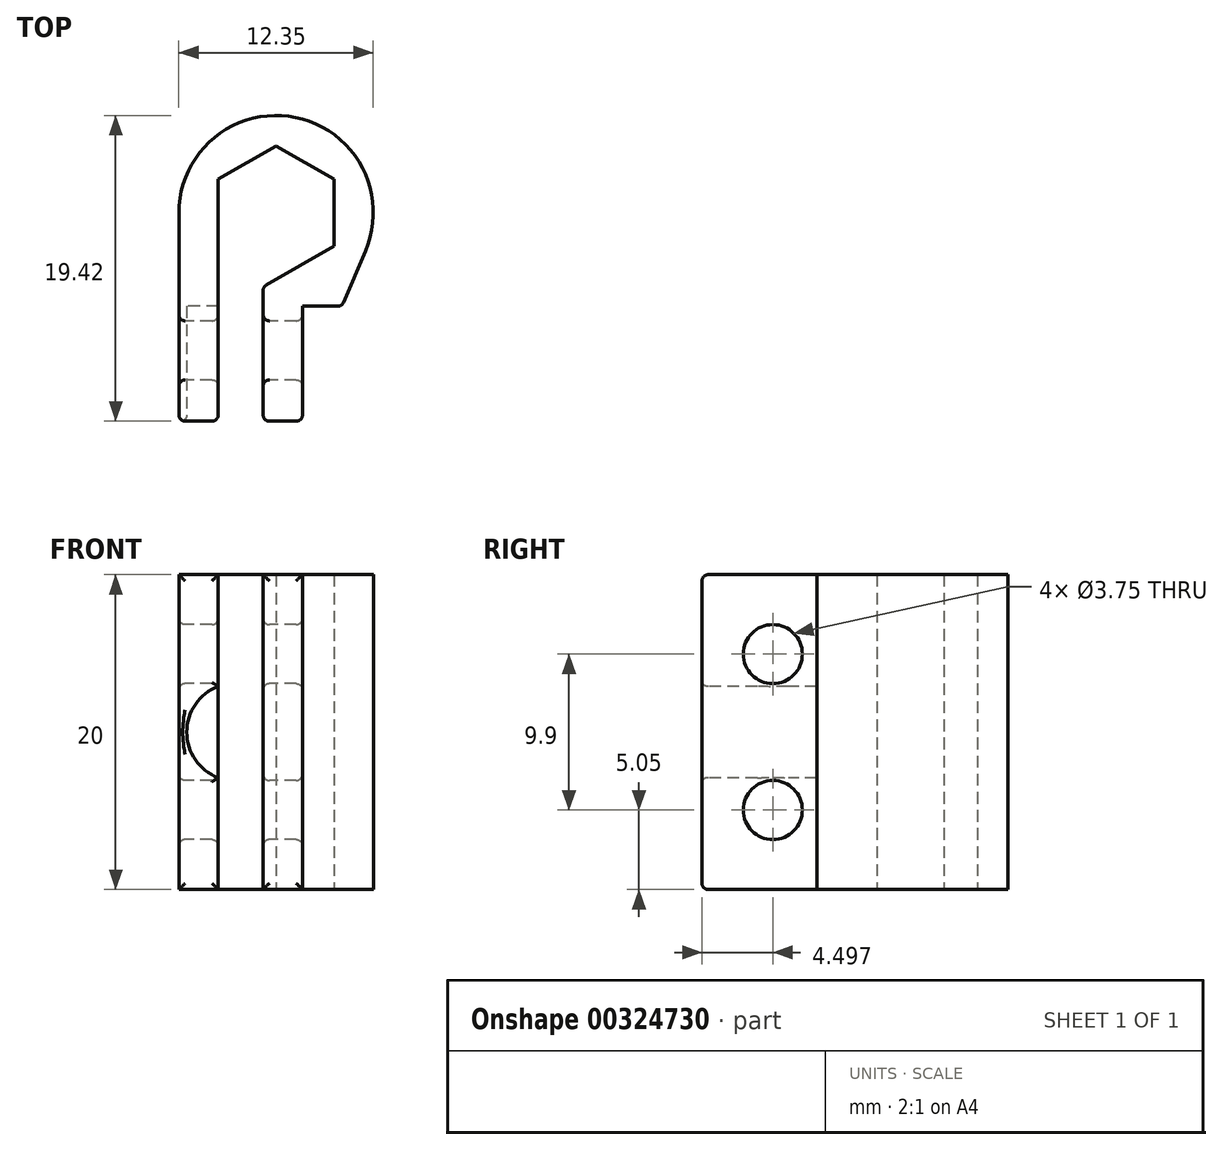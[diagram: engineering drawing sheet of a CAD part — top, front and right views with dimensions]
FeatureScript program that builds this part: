
annotation { "Feature Type Name" : "Feature", "Feature Type Description" : "" }
export const myFeature = defineFeature(function(context is Context, id is Id, definition is map)
    precondition{}
    {
        {
            var Q0;
            Q0=qCreatedBy(makeId("Top.planeOp"),FACE);
            var sketch = newSketch(context, id + "F0", { "sketchPlane" : qUnion([Q0])});
            skCircle(sketch, "E0", {"center": v(0, 0) * mm, "radius": 3.67 * mm, "construction": true});
            skArc(sketch, "E1.0", {"start": v(-0.82, -6.12) * mm, "mid": v(2.32, 5.72) * mm, "end": v(-3.67, -4.96) * mm});
            skLineSegment(sketch, "E2", {"start": v(-6.17, 0) * mm, "end": v(-6.17, -13.24) * mm});
            skLineSegment(sketch, "E3", {"start": v(-6.17, -13.24) * mm, "end": v(-3.67, -13.24) * mm});
            skLineSegment(sketch, "E4", {"start": v(-3.67, -13.24) * mm, "end": v(-3.67, 0) * mm});
            skLineSegment(sketch, "E5", {"start": v(-3.67, -13.24) * mm, "end": v(-0.82, -13.24) * mm, "construction": true});
            skLineSegment(sketch, "E6", {"start": v(-0.82, -13.24) * mm, "end": v(-0.82, -4.72) * mm});
            skLineSegment(sketch, "E7", {"start": v(-0.82, -13.24) * mm, "end": v(1.67, -13.24) * mm});
            skLineSegment(sketch, "E8", {"start": v(1.68, -13.24) * mm, "end": v(1.68, -5.94) * mm});
            skPoint(sketch, "E9", {"position": v(-6.17, -10.24) * mm});
            skPoint(sketch, "E10", {"position": v(-6.17, -7.24) * mm});
            skPoint(sketch, "E11", {"position": v(-6.17, -8.74) * mm});
            skLineSegment(sketch, "E12", {"start": v(-6.17, -7.24) * mm, "end": v(-6.17, -10.24) * mm});
            skLineSegment(sketch, "E13", {"start": v(-6.17, -8.74) * mm, "end": v(1.68, -8.74) * mm, "construction": true});
            skPoint(sketch, "E14", {"position": v(1.68, -5.94) * mm});
            skPoint(sketch, "E15", {"position": v(1.68, -11.54) * mm});
            skLineSegment(sketch, "E16.0", {"start": v(-3.67, -2.12) * mm, "end": v(-3.67, 2.12) * mm});
            skLineSegment(sketch, "E16.1", {"start": v(-3.68, 2.12) * mm, "end": v(0, 4.24) * mm});
            skLineSegment(sketch, "E16.2", {"start": v(0, 4.24) * mm, "end": v(3.68, 2.12) * mm});
            skLineSegment(sketch, "E16.3", {"start": v(3.67, 2.12) * mm, "end": v(3.67, -2.12) * mm});
            skLineSegment(sketch, "E16.4", {"start": v(3.68, -2.12) * mm, "end": v(-0.82, -4.72) * mm});
            skPoint(sketch, "E16.0.midPoint", {"position": v(-3.67, 0) * mm});
            skLineSegment(sketch, "E17", {"start": v(1.67, -5.94) * mm, "end": v(4.17, -5.94) * mm});
            skLineSegment(sketch, "E18", {"start": v(4.17, -5.94) * mm, "end": v(5.68, -2.43) * mm});
            skSolve(sketch);
        }
        {
            var Q0;
            Q0=qSketchRegion(id+"F0",true);
            extrude(context, id + "F1", {"entities" : qUnion([Q0]), "depth" : 20 * mm});
        }
        {
            var Q0;
            Q0=makeQuery(id+"F1.opExtrude","SWEPT_FACE",FACE,{"disambiguationData":[OSD([sQuery(id+"F0.wireOp",EDGE,"E2"),sQuery(id+"F0.wireOp",EDGE,"E12")])]});
            var sketch = newSketch(context, id + "F2", { "sketchPlane" : qUnion([Q0])});
            skPoint(sketch, "E19.0", {"position": v(8.74, 0) * mm});
            skLineSegment(sketch, "E20", {"start": v(8.74, 0) * mm, "end": v(8.74, 20) * mm, "construction": true});
            skPoint(sketch, "E21", {"position": v(8.74, 10) * mm});
            skPoint(sketch, "E22", {"position": v(8.74, 12.9) * mm});
            skPoint(sketch, "E23", {"position": v(8.74, 7.1) * mm});
            skPoint(sketch, "E24", {"position": v(8.74, 17) * mm});
            skPoint(sketch, "E25", {"position": v(8.74, 3) * mm});
            skPoint(sketch, "E26", {"position": v(8.74, 14.95) * mm});
            skPoint(sketch, "E27", {"position": v(8.74, 5.05) * mm});
            skCircle(sketch, "E28", {"center": v(8.74, 14.95) * mm, "radius": 1.88 * mm});
            skCircle(sketch, "E29", {"center": v(8.74, 5.05) * mm, "radius": 1.88 * mm});
            skSolve(sketch);
        }
        {
            var Q0;
            Q0=makeQuery(id+"F2.imprint","IMPRINT",FACE,{"disambiguationData":[TD([[makeQuery(id+"F2.imprint","IMPRINT",EDGE,{"derivedFrom":sQuery(id+"F2.wireOp",EDGE,"E28")}),1.0]])]});
            var Q1;
            Q1=makeQuery(id+"F2.imprint","IMPRINT",FACE,{"disambiguationData":[TD([[makeQuery(id+"F2.imprint","IMPRINT",EDGE,{"derivedFrom":sQuery(id+"F2.wireOp",EDGE,"E29")}),1.0]])]});
            extrude(context, id + "F3", {"entities" : qUnion([Q0, Q1]), "operationType" : NewBodyOperationType.REMOVE, "endBound" : BoundingType.THROUGH_ALL, "oppositeDirection" : true, "depth" : 25.4 * mm});
        }
        {
            var Q0;
            Q0=makeQuery(id+"F1.opExtrude","SWEPT_FACE",FACE,{"disambiguationData":[OSD([sQuery(id+"F0.wireOp",EDGE,"E3")])]});
            var sketch = newSketch(context, id + "F4", { "sketchPlane" : qUnion([Q0])});
            skPoint(sketch, "E30.0", {"position": v(-6.17, 7.1) * mm});
            skPoint(sketch, "E30.1", {"position": v(-6.17, 12.9) * mm});
            skPoint(sketch, "E30.2", {"position": v(-6.17, 10) * mm});
            skLineSegment(sketch, "E31", {"start": v(-6.17, 10) * mm, "end": v(-3.67, 10) * mm, "construction": true});
            skLineSegment(sketch, "E32", {"start": v(-6.17, 12.9) * mm, "end": v(-3.67, 12.9) * mm, "construction": true});
            skLineSegment(sketch, "E33", {"start": v(-6.17, 7.1) * mm, "end": v(-3.67, 7.1) * mm});
            skArc(sketch, "E34", {"start": v(-3.67, 12.9) * mm, "mid": v(-5.67, 10) * mm, "end": v(-3.67, 7.1) * mm});
            skPoint(sketch, "E35", {"position": v(-5.67, 10) * mm});
            skSolve(sketch);
        }
        {
            var Q0;
            {var subQ0=sQuery(id+"F4.wireOp",EDGE,"E34");Q0=makeQuery(id+"F4.imprint","IMPRINT",FACE,{"disambiguationData":[TD([[makeQuery(id+"F4.imprint","IMPRINT",EDGE,{"derivedFrom":subQ0}),1.0]])]});}
            var Q1;
            Q1=makeQuery(id+"F1.opExtrude","SWEPT_FACE",FACE,{"disambiguationData":[OSD([sQuery(id+"F0.wireOp",EDGE,"E17")])]});
            extrude(context, id + "F5", {"entities" : qUnion([Q0]), "operationType" : NewBodyOperationType.REMOVE, "endBound" : BoundingType.UP_TO_SURFACE, "oppositeDirection" : true, "endBoundEntityFace" : qUnion([Q1]), "depth" : 25.4 * mm});
        }
        {
            var Q0;
            Q0=makeQuery(id+"F3.boolean.opBoolean","COPY",FACE,{"disambiguationData":[TD([makeQuery(id+"F1.opExtrude","SWEPT_FACE",FACE,{"disambiguationData":[OSD([sQuery(id+"F0.wireOp",EDGE,"E6")])]})])],"derivedFrom":makeQuery(id+"F3.opExtrude","SWEPT_FACE",FACE,{"disambiguationData":[OSD([sQuery(id+"F2.wireOp",EDGE,"E28")])]})});
            var Q1;
            Q1=makeQuery(id+"F3.boolean.opBoolean","COPY",FACE,{"disambiguationData":[TD([makeQuery(id+"F1.opExtrude","SWEPT_FACE",FACE,{"disambiguationData":[OSD([sQuery(id+"F0.wireOp",EDGE,"E6")])]})])],"derivedFrom":makeQuery(id+"F3.opExtrude","SWEPT_FACE",FACE,{"disambiguationData":[OSD([sQuery(id+"F2.wireOp",EDGE,"E29")])]})});
            var Q2;
            Q2=makeQuery(id+"F3.boolean.opBoolean","COPY",FACE,{"disambiguationData":[TD([makeQuery(id+"F1.opExtrude","SWEPT_FACE",FACE,{"disambiguationData":[OSD([sQuery(id+"F0.wireOp",EDGE,"E2"),sQuery(id+"F0.wireOp",EDGE,"E12")])]})])],"derivedFrom":makeQuery(id+"F3.opExtrude","SWEPT_FACE",FACE,{"disambiguationData":[OSD([sQuery(id+"F2.wireOp",EDGE,"E29")])]})});
            var Q3;
            Q3=makeQuery(id+"F3.boolean.opBoolean","COPY",FACE,{"disambiguationData":[TD([makeQuery(id+"F1.opExtrude","SWEPT_FACE",FACE,{"disambiguationData":[OSD([sQuery(id+"F0.wireOp",EDGE,"E2"),sQuery(id+"F0.wireOp",EDGE,"E12")])]})])],"derivedFrom":makeQuery(id+"F3.opExtrude","SWEPT_FACE",FACE,{"disambiguationData":[OSD([sQuery(id+"F2.wireOp",EDGE,"E28")])]})});
            var Q4;
            Q4=makeQuery(id+"F1.opExtrude","SWEPT_EDGE",EDGE,{"disambiguationData":[OSD([sQuery(id+"F0.wireOp",EDGE,"E6"),sQuery(id+"F0.wireOp",EDGE,"E16.4")])]});
            var Q5;
            Q5=makeQuery(id+"F1.opExtrude","SWEPT_EDGE",EDGE,{"disambiguationData":[OSD([sQuery(id+"F0.wireOp",EDGE,"E17"),sQuery(id+"F0.wireOp",EDGE,"E18")])]});
            var Q6;
            Q6=makeQuery(id+"F1.opExtrude","SWEPT_FACE",FACE,{"disambiguationData":[OSD([sQuery(id+"F0.wireOp",EDGE,"E7")])]});
            var Q7;
            Q7=makeQuery(id+"F1.opExtrude","SWEPT_FACE",FACE,{"disambiguationData":[OSD([sQuery(id+"F0.wireOp",EDGE,"E3")])]});
            fillet(context, id + "F6", {"entities" : qUnion([Q0, Q1, Q2, Q3, Q4, Q5, Q6, Q7]), "radius" : 0.4 * mm, "tangentPropagation" : true, "allowEdgeOverflow" : false});
        }
    });
